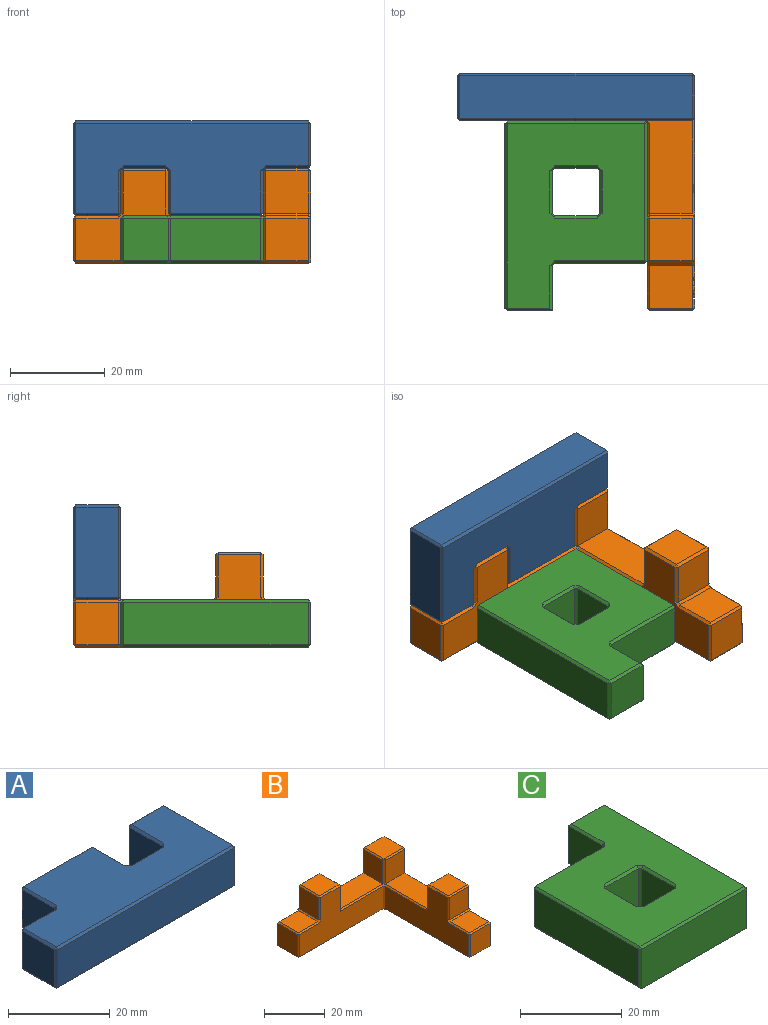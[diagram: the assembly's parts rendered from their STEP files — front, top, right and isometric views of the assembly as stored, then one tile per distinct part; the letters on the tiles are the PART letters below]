
ASSEMBLY  parts=3 mates=1
PART A: 62 faces, bbox 50x20x10 mm
  f0: plane 49x19mm, normal (0,0,1), area 722.5mm2, adj f15,f16,f25,f26,f32,f35,f36,f45
  f1: plane 49x19mm, normal (0,0,-1), area 722.5mm2, adj f18,f19,f28,f29,f33,f38,f39,f48
  f2: plane 9x9mm, normal (-1,0,0), area 81mm2, adj f12,f16,f17,f18
  f3: plane 49x9mm, normal (0,-1,0), area 441mm2, adj f12,f15,f19,f20
  f4: plane 19x9mm, normal (1,0,0), area 171mm2, adj f20,f25,f29,f30
  f5: plane 9x9mm, normal (0,1,0), area 81mm2, adj f30,f35,f39,f40
  f6: plane 9x9mm, normal (-1,0,0), area 81mm2, adj f40,f45,f49,f50
  f7: plane 9x9mm, normal (0,1,0), area 81mm2, adj f50,f55,f58,f61
  f8: plane 9x9mm, normal (1,0,0), area 81mm2, adj f47,f56,f57,f61
  f9: plane 19x9mm, normal (0,1,0), area 171mm2, adj f37,f46,f47,f48
  f10: plane 9x9mm, normal (-1,0,0), area 81mm2, adj f27,f36,f37,f38
  f11: plane 9x9mm, normal (0,1,0), area 81mm2, adj f17,f26,f27,f28
  f12: plane 9x0.5mm, normal (-0.71,-0.71,0), area 6.4mm2, adj f2,f3,f13,f14
  f13: plane 0.5x0.5mm, normal (-0.58,-0.58,0.58), area 0.2mm2, adj f12,f15,f16
  f14: plane 0.5x0.5mm, normal (-0.58,-0.58,-0.58), area 0.2mm2, adj f12,f18,f19
  f15: plane 49x0.5mm, normal (0,-0.71,0.71), area 34.6mm2, adj f0,f3,f13,f21
  f16: plane 9x0.5mm, normal (-0.71,0,0.71), area 6.4mm2, adj f0,f2,f13,f22
  f17: plane 9x0.5mm, normal (-0.71,0.71,0), area 6.4mm2, adj f2,f11,f22,f23
  f18: plane 9x0.5mm, normal (-0.71,0,-0.71), area 6.4mm2, adj f1,f2,f14,f23
  f19: plane 49x0.5mm, normal (0,-0.71,-0.71), area 34.6mm2, adj f1,f3,f14,f24
  f20: plane 9x0.5mm, normal (0.71,-0.71,0), area 6.4mm2, adj f3,f4,f21,f24
  f21: plane 0.5x0.5mm, normal (0.58,-0.58,0.58), area 0.2mm2, adj f15,f20,f25
  f22: plane 0.5x0.5mm, normal (-0.58,0.58,0.58), area 0.2mm2, adj f16,f17,f26
  f23: plane 0.5x0.5mm, normal (-0.58,0.58,-0.58), area 0.2mm2, adj f17,f18,f28
  f24: plane 0.5x0.5mm, normal (0.58,-0.58,-0.58), area 0.2mm2, adj f19,f20,f29
  f25: plane 19x0.5mm, normal (0.71,0,0.71), area 13.4mm2, adj f0,f4,f21,f31
  f26: plane 9x0.5mm, normal (0,0.71,0.71), area 6.4mm2, adj f0,f11,f22,f32
  f27: plane 9x0.5mm, normal (-0.71,0.71,0), area 6.4mm2, adj f10,f11,f32,f33
  f28: plane 9x0.5mm, normal (0,0.71,-0.71), area 6.4mm2, adj f1,f11,f23,f33
  f29: plane 19x0.5mm, normal (0.71,0,-0.71), area 13.4mm2, adj f1,f4,f24,f34
  f30: plane 9x0.5mm, normal (0.71,0.71,0), area 6.4mm2, adj f4,f5,f31,f34
  f31: plane 0.5x0.5mm, normal (0.58,0.58,0.58), area 0.2mm2, adj f25,f30,f35
  f32: plane 1x1mm, normal (-0.58,0.58,0.58), area 0.6mm2, adj f0,f26,f27,f36
  f33: plane 1x1mm, normal (-0.58,0.58,-0.58), area 0.6mm2, adj f1,f27,f28,f38
  f34: plane 0.5x0.5mm, normal (0.58,0.58,-0.58), area 0.2mm2, adj f29,f30,f39
  f35: plane 9x0.5mm, normal (0,0.71,0.71), area 6.4mm2, adj f0,f5,f31,f41
  f36: plane 9x0.5mm, normal (-0.71,0,0.71), area 6.4mm2, adj f0,f10,f32,f42
  f37: plane 9x0.5mm, normal (-0.71,0.71,0), area 6.4mm2, adj f9,f10,f42,f43
  f38: plane 9x0.5mm, normal (-0.71,0,-0.71), area 6.4mm2, adj f1,f10,f33,f43
  f39: plane 9x0.5mm, normal (0,0.71,-0.71), area 6.4mm2, adj f1,f5,f34,f44
  f40: plane 9x0.5mm, normal (-0.71,0.71,0), area 6.4mm2, adj f5,f6,f41,f44
  f41: plane 0.5x0.5mm, normal (-0.58,0.58,0.58), area 0.2mm2, adj f35,f40,f45
  f42: plane 0.5x0.5mm, normal (-0.58,0.58,0.58), area 0.2mm2, adj f36,f37,f46
  f43: plane 0.5x0.5mm, normal (-0.58,0.58,-0.58), area 0.2mm2, adj f37,f38,f48
  f44: plane 0.5x0.5mm, normal (-0.58,0.58,-0.58), area 0.2mm2, adj f39,f40,f49
  f45: plane 9x0.5mm, normal (-0.71,0,0.71), area 6.4mm2, adj f0,f6,f41,f51
  f46: plane 19x0.5mm, normal (0,0.71,0.71), area 13.4mm2, adj f0,f9,f42,f52
  f47: plane 9x0.5mm, normal (0.71,0.71,0), area 6.4mm2, adj f8,f9,f52,f53
  f48: plane 19x0.5mm, normal (0,0.71,-0.71), area 13.4mm2, adj f1,f9,f43,f53
  f49: plane 9x0.5mm, normal (-0.71,0,-0.71), area 6.4mm2, adj f1,f6,f44,f54
  f50: plane 9x0.5mm, normal (-0.71,0.71,0), area 6.4mm2, adj f6,f7,f51,f54
  f51: plane 1x1mm, normal (-0.58,0.58,0.58), area 0.6mm2, adj f0,f45,f50,f55
  f52: plane 0.5x0.5mm, normal (0.58,0.58,0.58), area 0.2mm2, adj f46,f47,f56
  f53: plane 0.5x0.5mm, normal (0.58,0.58,-0.58), area 0.2mm2, adj f47,f48,f57
  f54: plane 1x1mm, normal (-0.58,0.58,-0.58), area 0.6mm2, adj f1,f49,f50,f58
  f55: plane 9x0.5mm, normal (0,0.71,0.71), area 6.4mm2, adj f0,f7,f51,f59
  f56: plane 9x0.5mm, normal (0.71,0,0.71), area 6.4mm2, adj f0,f8,f52,f59
  f57: plane 9x0.5mm, normal (0.71,0,-0.71), area 6.4mm2, adj f1,f8,f53,f60
  f58: plane 9x0.5mm, normal (0,0.71,-0.71), area 6.4mm2, adj f1,f7,f54,f60
  f59: plane 1x1mm, normal (0.58,0.58,0.58), area 0.6mm2, adj f0,f55,f56,f61
  f60: plane 1x1mm, normal (0.58,0.58,-0.58), area 0.6mm2, adj f1,f57,f58,f61
  f61: plane 9x0.5mm, normal (0.71,0.71,0), area 6.4mm2, adj f7,f8,f59,f60
PART B: 151 faces, bbox 50x50x20 mm
  f0: plane 9.63x0.5mm, normal (0,-0.71,-0.71), area 6.6mm2, adj f12,f17,f34,f49,f53,f114,f136
  f1: plane 0.51x0.51mm, normal (0,0,1), area 0.1mm2, adj f4,f5,f89
  f2: plane 21x0.75mm, normal (0,0.71,0.71), area 14.6mm2, adj f10,f15,f82,f86,f91
  f3: plane 19.25x0.5mm, normal (0.71,0.71,0), area 13.5mm2, adj f7,f10,f83,f84,f97
  f4: plane 10x0.51mm, normal (0,1,0), area 0.2mm2, adj f1,f15,f87,f89,f90
  f5: plane 10x0.51mm, normal (1,0,0), area 0.2mm2, adj f1,f15,f88,f89,f94
  f6: plane 9x9mm, normal (0,0,1), area 81mm2, adj f90,f94,f95,f98
  f7: plane 24.8x19mm, normal (1,0,0), area 304.6mm2, adj f3,f83,f85,f93,f98,f100
  f8: plane 7.23x3.69mm, normal (1,0,0), area 12.3mm2, adj f85,f103,f104,f105,f106
  f9: plane 39x19mm, normal (-1,0,0), area 442mm2, adj f37,f38,f42,f45,f49,f52,f53,f57
  f10: plane 49x19mm, normal (0,1,0), area 621.5mm2, adj f2,f3,f61,f69,f72,f76,f80,f82
  f11: plane 19.01x14.34mm, normal (1,0,0), area 148.2mm2, adj f24,f28,f29,f30,f31,f33,f40,f51
  f12: plane 49x49mm, normal (0,0,-1), area 801.5mm2, adj f0,f27,f28,f29,f53,f54,f56,f58
  f13: plane 7x3.65mm, normal (1,0,0), area 12.6mm2, adj f27,f101,f108,f109,f110,f111
  f14: plane 8.84x1.87mm, normal (1,0,0), area 8.2mm2, adj f33,f34,f114
  f15: plane 29x29mm, normal (0,0,1), area 351.4mm2, adj f2,f4,f5,f51,f62,f66,f70,f85
  f16: plane 9x9mm, normal (0,0,1), area 81mm2, adj f32,f33,f42,f43
  f17: plane 9x9mm, normal (0,-1,0), area 81mm2, adj f0,f34,f43,f49
  f18: plane 9x9mm, normal (0,0,1), area 81mm2, adj f59,f60,f68,f69
  f19: plane 39x19mm, normal (0,-1,0), area 441.5mm2, adj f48,f54,f59,f63,f64,f67,f70,f73
  f20: plane 9x9mm, normal (-1,0,0), area 81mm2, adj f48,f56,f60,f61
  f21: plane 9x9mm, normal (-1,0,0), area 81mm2, adj f67,f68,f75,f76
  f22: plane 9x9mm, normal (1,0,0), area 81mm2, adj f73,f79,f82,f86
  f23: plane 9x9mm, normal (0,0,1), area 81mm2, adj f74,f75,f79,f80
  f24: plane 9.5x9mm, normal (0,1,0), area 85.5mm2, adj f11,f44,f51,f52
  f25: plane 9x9mm, normal (0,-1,0), area 81mm2, adj f31,f32,f36,f37
  f26: plane 9x9mm, normal (0,0,1), area 81mm2, adj f36,f40,f44,f45
  f27: plane 3.91x0.5mm, normal (0.71,0,-0.71), area 2.7mm2, adj f12,f13,f101,f108
  f28: plane 2.09x0.5mm, normal (0.71,0,-0.71), area 1.4mm2, adj f11,f12,f99,f138
  f29: plane 5.18x0.5mm, normal (0.71,0,-0.71), area 2.5mm2, adj f11,f12,f113,f137
  f30: plane 1x1mm, normal (0.58,-0.58,0.58), area 0.6mm2, adj f11,f31,f32,f33
  f31: plane 9x0.5mm, normal (0.71,-0.71,0), area 6.4mm2, adj f11,f25,f30,f35
  f32: plane 9x0.5mm, normal (0,-0.71,0.71), area 6.4mm2, adj f16,f25,f30,f38
  f33: plane 9x0.5mm, normal (0.71,0,0.71), area 3.8mm2, adj f11,f14,f16,f30,f39,f114,f132,f134
  f34: plane 9.38x0.5mm, normal (0.71,-0.71,0), area 6.5mm2, adj f0,f14,f17,f39,f114
  f35: plane 0.5x0.5mm, normal (0.58,-0.58,0.58), area 0.2mm2, adj f31,f36,f40
  f36: plane 9x0.5mm, normal (0,-0.71,0.71), area 6.4mm2, adj f25,f26,f35,f41
  f37: plane 9x0.5mm, normal (-0.71,-0.71,0), area 6.4mm2, adj f9,f25,f38,f41
  f38: plane 1x1mm, normal (-0.58,-0.58,0.58), area 0.6mm2, adj f9,f32,f37,f42
  f39: plane 0.5x0.5mm, normal (0.58,-0.58,0.58), area 0.2mm2, adj f33,f34,f43
  f40: plane 9.5x0.5mm, normal (0.71,0,0.71), area 6.5mm2, adj f11,f26,f35,f44
  f41: plane 0.5x0.5mm, normal (-0.58,-0.58,0.58), area 0.2mm2, adj f36,f37,f45
  f42: plane 9x0.5mm, normal (-0.71,0,0.71), area 6.4mm2, adj f9,f16,f38,f46
  f43: plane 9x0.5mm, normal (0,-0.71,0.71), area 6.4mm2, adj f16,f17,f39,f46
  f44: plane 9.5x0.5mm, normal (0,0.71,0.71), area 6.5mm2, adj f24,f26,f40,f47
  f45: plane 9x0.5mm, normal (-0.71,0,0.71), area 6.4mm2, adj f9,f26,f41,f47
  f46: plane 0.5x0.5mm, normal (-0.58,-0.58,0.58), area 0.2mm2, adj f42,f43,f49
  f47: plane 0.5x0.5mm, normal (-0.58,0.58,0.58), area 0.2mm2, adj f44,f45,f52
  f48: plane 9x0.5mm, normal (-0.71,-0.71,0), area 6.4mm2, adj f19,f20,f50,f55
  f49: plane 9.25x0.5mm, normal (-0.71,-0.71,0), area 6.5mm2, adj f0,f9,f17,f46,f53
  f50: plane 0.5x0.5mm, normal (-0.58,-0.58,-0.58), area 0.2mm2, adj f48,f54,f56
  f51: plane 9.5x0.58mm, normal (0,0.71,0.71), area 6.8mm2, adj f11,f15,f24,f57,f85,f107
  f52: plane 9x0.5mm, normal (-0.71,0.71,0), area 6.4mm2, adj f9,f24,f47,f57
  f53: plane 39.25x0.5mm, normal (-0.71,0,-0.71), area 27.7mm2, adj f0,f9,f12,f49,f58
  f54: plane 39x0.5mm, normal (0,-0.71,-0.71), area 27.6mm2, adj f12,f19,f50,f58
  f55: plane 0.5x0.5mm, normal (-0.58,-0.58,0.58), area 0.2mm2, adj f48,f59,f60
  f56: plane 9.25x0.5mm, normal (-0.71,0,-0.71), area 6.5mm2, adj f12,f20,f50,f61,f84
  f57: plane 1x1mm, normal (-0.58,0.58,0.58), area 0.6mm2, adj f9,f51,f52,f62
  f58: plane 1x1mm, normal (-0.58,-0.58,-0.58), area 0.6mm2, adj f12,f53,f54,f63
  f59: plane 9x0.5mm, normal (0,-0.71,0.71), area 6.4mm2, adj f18,f19,f55,f64
  f60: plane 9x0.5mm, normal (-0.71,0,0.71), area 6.4mm2, adj f18,f20,f55,f65
  f61: plane 9.25x0.5mm, normal (-0.71,0.71,0), area 6.5mm2, adj f10,f20,f56,f65,f84
  f62: plane 19x0.5mm, normal (-0.71,0,0.71), area 13.4mm2, adj f9,f15,f57,f66
  f63: plane 9x0.5mm, normal (-0.71,-0.71,0), area 6.4mm2, adj f9,f19,f58,f66
  f64: plane 1x1mm, normal (-0.58,-0.58,0.58), area 0.6mm2, adj f19,f59,f67,f68
  f65: plane 0.5x0.5mm, normal (-0.58,0.58,0.58), area 0.2mm2, adj f60,f61,f69
  f66: plane 1x1mm, normal (-0.58,-0.58,0.58), area 0.6mm2, adj f15,f62,f63,f70
  f67: plane 9x0.5mm, normal (-0.71,-0.71,0), area 6.4mm2, adj f19,f21,f64,f71
  f68: plane 9x0.5mm, normal (-0.71,0,0.71), area 6.4mm2, adj f18,f21,f64,f72
  f69: plane 9x0.5mm, normal (0,0.71,0.71), area 6.4mm2, adj f10,f18,f65,f72
  f70: plane 20x0.75mm, normal (0,-0.71,0.71), area 14.1mm2, adj f15,f19,f66,f73,f86
  f71: plane 0.5x0.5mm, normal (-0.58,-0.58,0.58), area 0.2mm2, adj f67,f74,f75
  f72: plane 1x1mm, normal (-0.58,0.58,0.58), area 0.6mm2, adj f10,f68,f69,f76
  f73: plane 10x0.75mm, normal (0.71,-0.71,0), area 7mm2, adj f19,f22,f70,f77,f86
  f74: plane 9x0.5mm, normal (0,-0.71,0.71), area 6.4mm2, adj f19,f23,f71,f77
  f75: plane 9x0.5mm, normal (-0.71,0,0.71), area 6.4mm2, adj f21,f23,f71,f78
  f76: plane 9x0.5mm, normal (-0.71,0.71,0), area 6.4mm2, adj f10,f21,f72,f78
  f77: plane 0.5x0.5mm, normal (0.58,-0.58,0.58), area 0.2mm2, adj f73,f74,f79
  f78: plane 0.5x0.5mm, normal (-0.58,0.58,0.58), area 0.2mm2, adj f75,f76,f80
  f79: plane 9x0.5mm, normal (0.71,0,0.71), area 6.4mm2, adj f22,f23,f77,f81
  f80: plane 9x0.5mm, normal (0,0.71,0.71), area 6.4mm2, adj f10,f23,f78,f81
  f81: plane 0.5x0.5mm, normal (0.58,0.58,0.58), area 0.2mm2, adj f79,f80,f82
  f82: plane 10x0.75mm, normal (0.71,0.71,0), area 7mm2, adj f2,f10,f22,f81,f86
  f83: plane 25.15x0.5mm, normal (0.71,0,-0.71), area 17.7mm2, adj f3,f7,f12,f84,f100
  f84: plane 49.5x0.5mm, normal (0,0.71,-0.71), area 34.8mm2, adj f3,f10,f12,f56,f61,f83
  f85: plane 20x0.5mm, normal (0.71,0,0.71), area 12.5mm2, adj f7,f8,f15,f51,f93,f100,f102,f103
  f86: plane 9x0.5mm, normal (0.71,0,0.71), area 6.2mm2, adj f2,f15,f22,f70,f73,f82
  f87: plane 9.5x9mm, normal (-1,0,0), area 85.5mm2, adj f4,f15,f90,f91
  f88: plane 9.5x9mm, normal (0,-1,0), area 85.5mm2, adj f5,f15,f93,f94
  f89: plane 10x0.51mm, normal (-0.71,-0.71,0), area 7.1mm2, adj f1,f4,f5,f15
  f90: plane 9x0.5mm, normal (-0.71,0,0.71), area 6.4mm2, adj f4,f6,f87,f92
  f91: plane 10x0.5mm, normal (-0.71,0.71,0), area 6.9mm2, adj f2,f10,f87,f92
  f92: plane 0.5x0.5mm, normal (-0.58,0.58,0.58), area 0.2mm2, adj f90,f91,f95
  f93: plane 10x0.5mm, normal (0.71,-0.71,0), area 6.9mm2, adj f7,f85,f88,f96
  f94: plane 9x0.5mm, normal (0,-0.71,0.71), area 6.4mm2, adj f5,f6,f88,f96
  f95: plane 9x0.5mm, normal (0,0.71,0.71), area 6.4mm2, adj f6,f10,f92,f97
  f96: plane 0.5x0.5mm, normal (0.58,-0.58,0.58), area 0.2mm2, adj f93,f94,f98
  f97: plane 0.5x0.5mm, normal (0.58,0.58,0.58), area 0.2mm2, adj f3,f95,f98
  f98: plane 9x0.5mm, normal (0.71,0,0.71), area 6.4mm2, adj f6,f7,f96,f97
  f99: plane 9.92x2.09mm, normal (0,0.98,-0.21), area 4.9mm2, adj f11,f28,f107,f112
  f100: plane 9.92x2.1mm, normal (0,-0.98,0.21), area 4.9mm2, adj f7,f83,f85,f102,f112
  f101: plane 7.5x2.41mm, normal (0,0.95,0.31), area 3.8mm2, adj f13,f27,f111,f112
  f102: plane 1.86x0.08mm, normal (0,0,-1), area 0.2mm2, adj f85,f100,f103,f112
  f103: extruded ~5.83x1.22mm, area 2.9mm2, adj f8,f85,f102,f104,f112
  f104: extruded ~1.47x0.5mm, area 0.7mm2, adj f8,f103,f105,f112
  f105: plane 0.5x0.03mm, normal (0,0,-1), area 0mm2, adj f8,f104,f106,f112
  f106: plane 7.3x2.3mm, normal (0,-0.95,-0.3), area 3.7mm2, adj f8,f85,f105,f107,f112
  f107: plane 2.42x0.5mm, normal (0,0,-1), area 1mm2, adj f11,f51,f85,f99,f106,f112
  f108: plane 4.67x0.98mm, normal (0,-0.98,0.21), area 2.3mm2, adj f13,f27,f109,f112
  f109: extruded ~2.62x0.5mm, area 1.3mm2, adj f13,f108,f110,f112
  f110: plane 0.5x0.22mm, normal (0,-0.99,0.13), area 0.1mm2, adj f13,f109,f111,f112
  f111: plane 0.5x0.04mm, normal (0,0,1), area 0mm2, adj f13,f101,f110,f112
  f112: plane 10.19x9.92mm, normal (1,0,0), area 51.9mm2, adj f12,f99,f100,f101,f102,f103,f104,f105
  f113: extruded ~2.87x0.84mm, area 0.7mm2, adj f11,f29,f125,f136
  f114: plane 9.8x2.07mm, normal (0,0.98,-0.21), area 4.9mm2, adj f0,f14,f33,f34,f134,f136
  f115: plane 1.22x0.5mm, normal (0,0,-1), area 0.6mm2, adj f116,f135,f136,f149
  f116: plane 2.58x0.56mm, normal (0,-0.98,0.21), area 1.3mm2, adj f115,f117,f136,f149
  f117: plane 1.12x0.5mm, normal (0,0,1), area 0.6mm2, adj f116,f118,f136,f149
  f118: extruded ~1.24x1.1mm, area 1mm2, adj f117,f119,f136,f149
  f119: extruded ~1.09x0.5mm, area 0.6mm2, adj f118,f135,f136,f149
  f120: plane 1.01x0.5mm, normal (0,0,-1), area 0.5mm2, adj f121,f133,f136,f150
  f121: plane 2.21x0.5mm, normal (0,-0.98,0.21), area 1.1mm2, adj f120,f122,f136,f150
  f122: plane 1.03x0.5mm, normal (0,0,1), area 0.5mm2, adj f121,f123,f136,f150
  f123: extruded ~1.15x0.93mm, area 0.8mm2, adj f122,f124,f136,f150
  f124: extruded ~0.95x0.5mm, area 0.5mm2, adj f123,f133,f136,f150
  f125: extruded ~2.39x1.04mm, area 1.4mm2, adj f11,f113,f126,f136
  f126: extruded ~1.22x0.5mm, area 0.7mm2, adj f11,f125,f127,f136
  f127: extruded ~1.08x0.65mm, area 0.6mm2, adj f11,f126,f128,f136
  f128: plane 0.5x0.04mm, normal (0,-1,0), area 0mm2, adj f11,f127,f129,f136
  f129: extruded ~1.6x0.88mm, area 0.9mm2, adj f11,f128,f130,f136
  f130: extruded ~1.68x0.56mm, area 0.9mm2, adj f11,f129,f131,f136
  f131: extruded ~1.65x0.79mm, area 1mm2, adj f11,f130,f132,f136
  f132: extruded ~2.35x0.55mm, area 0.6mm2, adj f11,f33,f131,f134,f136
  f133: extruded ~1.23x0.5mm, area 0.6mm2, adj f120,f124,f136,f150
  f134: plane 2.89x0.08mm, normal (0,0,-1), area 0.2mm2, adj f33,f114,f132,f136
  f135: extruded ~1.24x0.5mm, area 0.7mm2, adj f115,f119,f136,f149
  f136: plane 9.92x8.1mm, normal (1,0,0), area 50.3mm2, adj f0,f12,f113,f114,f115,f116,f117,f118
  f137: plane 9.92x2.09mm, normal (0,0.98,-0.21), area 4.9mm2, adj f11,f29,f147,f148
  f138: plane 1.74x0.5mm, normal (0,-0.98,0.21), area 0.8mm2, adj f11,f28,f139,f148
  f139: plane 3.47x0.5mm, normal (0,0,-1), area 1.7mm2, adj f11,f138,f140,f148
  f140: plane 2.56x0.54mm, normal (0,-0.98,0.21), area 1.3mm2, adj f11,f139,f141,f148
  f141: plane 3.23x0.5mm, normal (0,0,1), area 1.6mm2, adj f11,f140,f142,f148
  f142: plane 1.72x0.5mm, normal (0,-0.98,0.21), area 0.9mm2, adj f11,f141,f143,f148
  f143: plane 3.24x0.5mm, normal (0,0,-1), area 1.6mm2, adj f11,f142,f144,f148
  f144: plane 2.18x0.5mm, normal (0,-0.98,0.2), area 1.1mm2, adj f11,f143,f145,f148
  f145: plane 3.47x0.5mm, normal (0,0,1), area 1.7mm2, adj f11,f144,f146,f148
  f146: plane 1.72x0.5mm, normal (0,-0.98,0.21), area 0.9mm2, adj f11,f145,f147,f148
  f147: plane 5.55x0.5mm, normal (0,0,-1), area 2.8mm2, adj f11,f137,f146,f148
  f148: plane 9.92x7.64mm, normal (1,0,0), area 38.1mm2, adj f12,f137,f138,f139,f140,f141,f142,f143
  f149: plane 2.91x2.58mm, normal (1,0,0), area 6.1mm2, adj f115,f116,f117,f118,f119,f135
  f150: plane 2.65x2.21mm, normal (1,0,0), area 4.8mm2, adj f120,f121,f122,f123,f124,f133
PART C: 48 faces, bbox 30x40x10 mm
  f0: plane 39x29mm, normal (0,0,1), area 812.5mm2, adj f13,f15,f16,f18,f19,f20,f21,f22
  f1: plane 39.5x29mm, normal (0,0,-1), area 846.5mm2, adj f4,f7,f8,f9,f10,f12,f14,f17
  f2: plane 19x9mm, normal (0,1,0), area 171mm2, adj f24,f25,f31,f32
  f3: plane 29x9mm, normal (-1,0,0), area 261mm2, adj f24,f28,f33,f34
  f4: plane 29x9.5mm, normal (0,-1,0), area 275.5mm2, adj f1,f33,f40,f46
  f5: plane 39x9mm, normal (1,0,0), area 351mm2, adj f41,f42,f46,f47
  f6: plane 9.5x9mm, normal (0,1,0), area 85.5mm2, adj f11,f35,f42,f43
  f7: plane 9.5x9mm, normal (1,0,0), area 85.5mm2, adj f1,f12,f14,f15
  f8: plane 9.5x9mm, normal (0,-1,0), area 85.5mm2, adj f1,f14,f20,f23
  f9: plane 9.5x9mm, normal (-1,0,0), area 85.5mm2, adj f1,f17,f21,f23
  f10: plane 9.5x9mm, normal (0,1,0), area 85.5mm2, adj f1,f12,f16,f17
  f11: plane 9.5x9mm, normal (-1,0,0), area 85.5mm2, adj f6,f30,f31,f39
  f12: plane 9.5x0.5mm, normal (0.71,0.71,0), area 6.7mm2, adj f1,f7,f10,f13
  f13: plane 1x1mm, normal (0.58,0.58,0.58), area 0.6mm2, adj f0,f12,f15,f16
  f14: plane 9.5x0.5mm, normal (0.71,-0.71,0), area 6.7mm2, adj f1,f7,f8,f18
  f15: plane 9x0.5mm, normal (0.71,0,0.71), area 6.4mm2, adj f0,f7,f13,f18
  f16: plane 9x0.5mm, normal (0,0.71,0.71), area 6.4mm2, adj f0,f10,f13,f19
  f17: plane 9.5x0.5mm, normal (-0.71,0.71,0), area 6.7mm2, adj f1,f9,f10,f19
  f18: plane 1x1mm, normal (0.58,-0.58,0.58), area 0.6mm2, adj f0,f14,f15,f20
  f19: plane 1x1mm, normal (-0.58,0.58,0.58), area 0.6mm2, adj f0,f16,f17,f21
  f20: plane 9x0.5mm, normal (0,-0.71,0.71), area 6.4mm2, adj f0,f8,f18,f22
  f21: plane 9x0.5mm, normal (-0.71,0,0.71), area 6.4mm2, adj f0,f9,f19,f22
  f22: plane 1x1mm, normal (-0.58,-0.58,0.58), area 0.6mm2, adj f0,f20,f21,f23
  f23: plane 9.5x0.5mm, normal (-0.71,-0.71,0), area 6.7mm2, adj f1,f8,f9,f22
  f24: plane 9x0.5mm, normal (-0.71,0.71,0), area 6.4mm2, adj f2,f3,f27,f29
  f25: plane 19x0.5mm, normal (0,0.71,0.71), area 13.4mm2, adj f0,f2,f26,f29
  f26: plane 1x1mm, normal (-0.58,0.58,0.58), area 0.6mm2, adj f0,f25,f30,f31
  f27: plane 0.5x0.5mm, normal (-0.58,0.58,-0.58), area 0.2mm2, adj f24,f28,f32
  f28: plane 29.5x0.5mm, normal (-0.71,0,-0.71), area 20.7mm2, adj f1,f3,f27,f33
  f29: plane 0.5x0.5mm, normal (-0.58,0.58,0.58), area 0.2mm2, adj f24,f25,f34
  f30: plane 9.5x0.5mm, normal (-0.71,0,0.71), area 6.5mm2, adj f0,f11,f26,f35
  f31: plane 9x0.5mm, normal (-0.71,0.71,0), area 6.4mm2, adj f2,f11,f26,f36
  f32: plane 19x0.5mm, normal (0,0.71,-0.71), area 13.4mm2, adj f1,f2,f27,f36
  f33: plane 9.5x0.5mm, normal (-0.71,-0.71,0), area 6.5mm2, adj f3,f4,f28,f37
  f34: plane 29x0.5mm, normal (-0.71,0,0.71), area 20.5mm2, adj f0,f3,f29,f37
  f35: plane 9.5x0.5mm, normal (0,0.71,0.71), area 6.5mm2, adj f0,f6,f30,f38
  f36: plane 1x1mm, normal (-0.58,0.58,-0.58), area 0.6mm2, adj f1,f31,f32,f39
  f37: plane 0.5x0.5mm, normal (-0.58,-0.58,0.58), area 0.2mm2, adj f33,f34,f40
  f38: plane 0.5x0.5mm, normal (0.58,0.58,0.58), area 0.2mm2, adj f35,f41,f42
  f39: plane 9.5x0.5mm, normal (-0.71,0,-0.71), area 6.5mm2, adj f1,f11,f36,f43
  f40: plane 29x0.5mm, normal (0,-0.71,0.71), area 20.5mm2, adj f0,f4,f37,f44
  f41: plane 39x0.5mm, normal (0.71,0,0.71), area 27.6mm2, adj f0,f5,f38,f44
  f42: plane 9x0.5mm, normal (0.71,0.71,0), area 6.4mm2, adj f5,f6,f38,f45
  f43: plane 9.5x0.5mm, normal (0,0.71,-0.71), area 6.5mm2, adj f1,f6,f39,f45
  f44: plane 0.5x0.5mm, normal (0.58,-0.58,0.58), area 0.2mm2, adj f40,f41,f46
  f45: plane 0.5x0.5mm, normal (0.58,0.58,-0.58), area 0.2mm2, adj f42,f43,f47
  f46: plane 9.5x0.5mm, normal (0.71,-0.71,0), area 6.5mm2, adj f4,f5,f44,f47
  f47: plane 39.5x0.5mm, normal (0.71,0,-0.71), area 27.8mm2, adj f1,f5,f45,f46
PLACE A rot(axis=(0,0.71,-0.71),180deg) t=(-1.76,4.96,112.01)mm
PLACE B t=(-50.04,-20.04,-9.78)mm
PLACE C rot(axis=(0,0,-1),180deg) t=(-132.54,35.53,-9.78)mm
MATE fastened A.f7 <-> B.f23  axis (0,0,-1) through (-60.04,-0.04,10.22)mm
